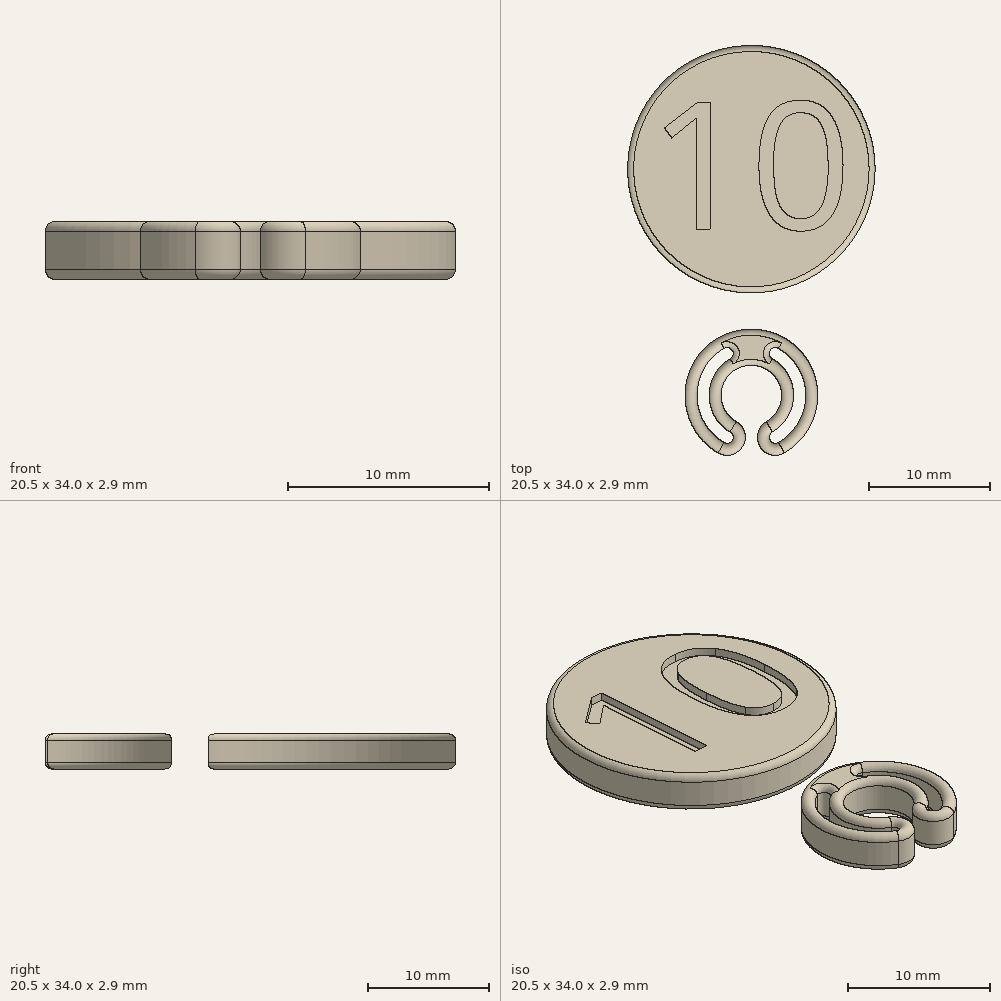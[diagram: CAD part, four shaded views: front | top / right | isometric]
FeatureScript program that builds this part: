
annotation { "Feature Type Name" : "Feature", "Feature Type Description" : "" }
export const myFeature = defineFeature(function(context is Context, id is Id, definition is map)
    precondition{}
    {
        {
            var Q0;
            Q0=qCreatedBy(makeId("Top.planeOp"),FACE);
            var sketch = newSketch(context, id + "F0", { "sketchPlane" : qUnion([Q0])});
            skCircle(sketch, "E0", {"center": v(0, 0) * mm, "radius": 10.25 * mm});
            skArc(sketch, "E1", {"start": v(1.25, -20.92) * mm, "mid": v(0, -16.25) * mm, "end": v(-1.25, -20.92) * mm});
            skArc(sketch, "E2", {"start": v(2.75, -23.51) * mm, "mid": v(0, -13.25) * mm, "end": v(-2.75, -23.51) * mm});
            skArc(sketch, "E3", {"start": v(-1.25, -20.92) * mm, "mid": v(-0.7, -22.96) * mm, "end": v(-2.75, -23.51) * mm});
            skArc(sketch, "E4", {"start": v(1.25, -20.92) * mm, "mid": v(0.7, -22.96) * mm, "end": v(2.75, -23.51) * mm});
            skArc(sketch, "E5", {"start": v(-2, -22.21) * mm, "mid": v(-4, -18.75) * mm, "end": v(-2, -15.29) * mm, "construction": true});
            skArc(sketch, "E6", {"start": v(2, -22.21) * mm, "mid": v(4, -18.75) * mm, "end": v(2, -15.29) * mm, "construction": true});
            skLineSegment(sketch, "E7", {"start": v(-2, -22.21) * mm, "end": v(2, -15.29) * mm, "construction": true});
            skLineSegment(sketch, "E8", {"start": v(2, -22.21) * mm, "end": v(-2, -15.29) * mm, "construction": true});
            skArc(sketch, "E9.0", {"start": v(2.25, -22.65) * mm, "mid": v(4.5, -18.75) * mm, "end": v(2.25, -14.85) * mm});
            skArc(sketch, "E10.0", {"start": v(-2.25, -22.65) * mm, "mid": v(-4.5, -18.75) * mm, "end": v(-2.25, -14.85) * mm});
            skArc(sketch, "E11.0", {"start": v(-1.75, -21.78) * mm, "mid": v(-3.5, -18.75) * mm, "end": v(-1.75, -15.72) * mm});
            skArc(sketch, "E12.0", {"start": v(1.75, -21.78) * mm, "mid": v(3.5, -18.75) * mm, "end": v(1.75, -15.72) * mm});
            skArc(sketch, "E13", {"start": v(-1.75, -15.72) * mm, "mid": v(-1.57, -15.04) * mm, "end": v(-2.25, -14.85) * mm});
            skArc(sketch, "E14", {"start": v(-2.25, -22.65) * mm, "mid": v(-1.57, -22.46) * mm, "end": v(-1.75, -21.78) * mm});
            skArc(sketch, "E15", {"start": v(1.75, -21.78) * mm, "mid": v(1.57, -22.46) * mm, "end": v(2.25, -22.65) * mm});
            skArc(sketch, "E16", {"start": v(2.25, -14.85) * mm, "mid": v(1.57, -15.04) * mm, "end": v(1.75, -15.72) * mm});
            skArc(sketch, "E17", {"start": v(-5, -8.95) * mm, "mid": v(-3.05, -11.75) * mm, "end": v(-4.04, -15.02) * mm});
            skArc(sketch, "E18", {"start": v(5, -8.95) * mm, "mid": v(3.05, -11.75) * mm, "end": v(4.04, -15.02) * mm});
            skSolve(sketch);
        }
        {
            var Q0;
            {var subQ0=sQuery(id+"F0.wireOp",EDGE,"E0");var subQ1=makeQuery(id+"F0.imprint","INTERSECT",VERTEX,{"derivedFrom":[subQ0,sQuery(id+"F0.wireOp",EDGE,"E17")]});Q0=makeQuery(id+"F0.imprint","IMPRINT",FACE,{"disambiguationData":[TD([[makeQuery(id+"F0.imprint","IMPRINT",EDGE,{"disambiguationData":[TD([[subQ1,-1.0]])],"derivedFrom":subQ0}),1.0]])]});}
            var Q1;
            {var subQ0=sQuery(id+"F0.wireOp",EDGE,"E17");Q1=makeQuery(id+"F0.imprint","IMPRINT",FACE,{"disambiguationData":[TD([[makeQuery(id+"F0.imprint","IMPRINT",EDGE,{"derivedFrom":subQ0}),1.0]])]});}
            var Q2;
            Q2=makeQuery(id+"F0.imprint","IMPRINT",FACE,{"disambiguationData":[TD([[makeQuery(id+"F0.imprint","IMPRINT",EDGE,{"derivedFrom":sQuery(id+"F0.wireOp",EDGE,"E1")}),-1.0]])]});
            extrude(context, id + "F1", {"entities" : qUnion([Q0, Q1, Q2]), "depth" : 2.9 * mm});
        }
        {
            var Q0;
            Q0=makeQuery(id+"F1.opExtrude","CAP_FACE",FACE,{"disambiguationData":[OSD([sQuery(id+"F0.wireOp",EDGE,"E0"),sQuery(id+"F0.wireOp",EDGE,"E1"),sQuery(id+"F0.wireOp",EDGE,"E2"),sQuery(id+"F0.wireOp",EDGE,"E3"),sQuery(id+"F0.wireOp",EDGE,"E4"),sQuery(id+"F0.wireOp",EDGE,"E9.0"),sQuery(id+"F0.wireOp",EDGE,"E10.0"),sQuery(id+"F0.wireOp",EDGE,"E11.0"),sQuery(id+"F0.wireOp",EDGE,"E12.0"),sQuery(id+"F0.wireOp",EDGE,"E13"),sQuery(id+"F0.wireOp",EDGE,"E14"),sQuery(id+"F0.wireOp",EDGE,"E15"),sQuery(id+"F0.wireOp",EDGE,"E16"),sQuery(id+"F0.wireOp",EDGE,"E17"),sQuery(id+"F0.wireOp",EDGE,"E18")])],"isStart":false});
            var sketch = newSketch(context, id + "F2", { "sketchPlane" : qUnion([Q0])});
            skText(sketch, "E19", { "text": "10", "fontName": "OpenSans-Regular.ttf"});
            const initialGuessF2  = {"E19": [-0.00856, -0.00499, 1, 0, 0.01063]};
            skSetInitialGuess(sketch, initialGuessF2);
            skSolve(sketch);
        }
        {
            var Q0;
            Q0 = qSketchRegion(id + "F2", true);
            extrude(context, id + "F3", {"entities" : qUnion([Q0]), "operationType" : NewBodyOperationType.REMOVE, "oppositeDirection" : true, "depth" : 0.6 * mm});
        }
        {
            var Q0;
            Q0=makeQuery(id+"F1.opExtrude","SWEPT_FACE",FACE,{"disambiguationData":[OSD([sQuery(id+"F0.wireOp",EDGE,"E0")])]});
            var Q1;
            Q1=makeQuery(id+"F1.opExtrude","SWEPT_FACE",FACE,{"disambiguationData":[OSD([sQuery(id+"F0.wireOp",EDGE,"E17")])]});
            var Q2;
            {var subQ0=sQuery(id+"F0.wireOp",EDGE,"E2");Q2=makeQuery(id+"F1.opExtrude","SWEPT_FACE",FACE,{"disambiguationData":[OSD([subQ0]),TDD([makeQuery(id+"F0.imprint","IMPRINT",EDGE,{"disambiguationData":[TD([[makeQuery(id+"F0.imprint","INTERSECT",VERTEX,{"derivedFrom":[subQ0,sQuery(id+"F0.wireOp",EDGE,"E3")]}),1.0]])],"derivedFrom":subQ0})])]});}
            var Q3;
            Q3=makeQuery(id+"F1.opExtrude","SWEPT_FACE",FACE,{"disambiguationData":[OSD([sQuery(id+"F0.wireOp",EDGE,"E3")])]});
            var Q4;
            Q4=makeQuery(id+"F1.opExtrude","SWEPT_FACE",FACE,{"disambiguationData":[OSD([sQuery(id+"F0.wireOp",EDGE,"E1")])]});
            var Q5;
            Q5=makeQuery(id+"F1.opExtrude","SWEPT_FACE",FACE,{"disambiguationData":[OSD([sQuery(id+"F0.wireOp",EDGE,"E4")])]});
            var Q6;
            {var subQ0=sQuery(id+"F0.wireOp",EDGE,"E2");Q6=makeQuery(id+"F1.opExtrude","SWEPT_FACE",FACE,{"disambiguationData":[OSD([subQ0]),TDD([makeQuery(id+"F0.imprint","IMPRINT",EDGE,{"disambiguationData":[TD([[makeQuery(id+"F0.imprint","INTERSECT",VERTEX,{"derivedFrom":[subQ0,sQuery(id+"F0.wireOp",EDGE,"E4")]}),-1.0]])],"derivedFrom":subQ0})])]});}
            var Q7;
            Q7=makeQuery(id+"F1.opExtrude","SWEPT_FACE",FACE,{"disambiguationData":[OSD([sQuery(id+"F0.wireOp",EDGE,"E18")])]});
            var Q8;
            Q8=makeQuery(id+"F1.opExtrude","SWEPT_FACE",FACE,{"disambiguationData":[OSD([sQuery(id+"F0.wireOp",EDGE,"E9.0")])]});
            var Q9;
            Q9=makeQuery(id+"F1.opExtrude","SWEPT_FACE",FACE,{"disambiguationData":[OSD([sQuery(id+"F0.wireOp",EDGE,"E12.0")])]});
            var Q10;
            Q10=makeQuery(id+"F1.opExtrude","SWEPT_FACE",FACE,{"disambiguationData":[OSD([sQuery(id+"F0.wireOp",EDGE,"E15")])]});
            var Q11;
            Q11=makeQuery(id+"F1.opExtrude","SWEPT_FACE",FACE,{"disambiguationData":[OSD([sQuery(id+"F0.wireOp",EDGE,"E16")])]});
            var Q12;
            Q12=makeQuery(id+"F1.opExtrude","SWEPT_FACE",FACE,{"disambiguationData":[OSD([sQuery(id+"F0.wireOp",EDGE,"E10.0")])]});
            var Q13;
            Q13=makeQuery(id+"F1.opExtrude","SWEPT_FACE",FACE,{"disambiguationData":[OSD([sQuery(id+"F0.wireOp",EDGE,"E13")])]});
            var Q14;
            Q14=makeQuery(id+"F1.opExtrude","SWEPT_FACE",FACE,{"disambiguationData":[OSD([sQuery(id+"F0.wireOp",EDGE,"E11.0")])]});
            var Q15;
            Q15=makeQuery(id+"F1.opExtrude","SWEPT_FACE",FACE,{"disambiguationData":[OSD([sQuery(id+"F0.wireOp",EDGE,"E14")])]});
            fillet(context, id + "F4", {"entities" : qUnion([Q0, Q1, Q2, Q3, Q4, Q5, Q6, Q7, Q8, Q9, Q10, Q11, Q12, Q13, Q14, Q15]), "radius" : 0.5 * mm, "tangentPropagation" : true, "allowEdgeOverflow" : false});
        }
    });
